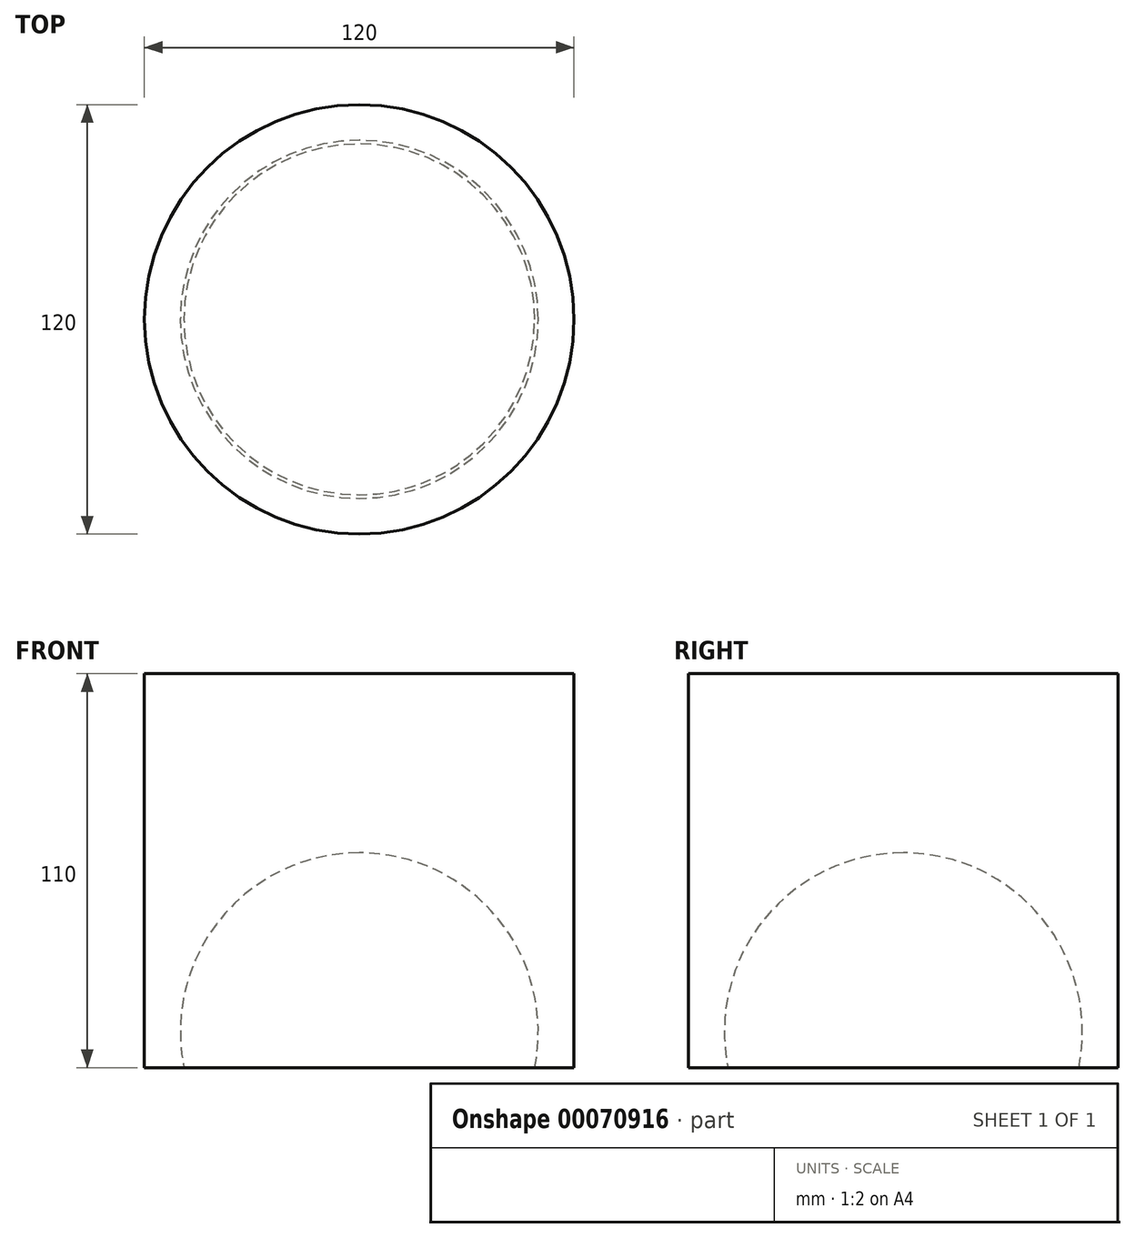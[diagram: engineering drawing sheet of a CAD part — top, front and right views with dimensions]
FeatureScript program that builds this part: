
annotation { "Feature Type Name" : "Feature", "Feature Type Description" : "" }
export const myFeature = defineFeature(function(context is Context, id is Id, definition is map)
    precondition{}
    {
        {
            var Q0;
            Q0=qCreatedBy(makeId("Front.planeOp"),FACE);
            var sketch = newSketch(context, id + "F0", { "sketchPlane" : qUnion([Q0])});
            skArc(sketch, "E0", {"start": v(-50, 0) * mm, "mid": v(0, 50) * mm, "end": v(50, 0) * mm});
            skLineSegment(sketch, "E1", {"start": v(-50, 0) * mm, "end": v(-60, 0) * mm});
            skLineSegment(sketch, "E2", {"start": v(-60, 0) * mm, "end": v(-60, 100) * mm});
            skLineSegment(sketch, "E3", {"start": v(50, 0) * mm, "end": v(60, 0) * mm});
            skLineSegment(sketch, "E4", {"start": v(60, 0) * mm, "end": v(60, 100) * mm});
            skLineSegment(sketch, "E5", {"start": v(60, 100) * mm, "end": v(-60, 100) * mm});
            skLineSegment(sketch, "E6", {"start": v(0, 0) * mm, "end": v(0, 119.73) * mm});
            skCircle(sketch, "E7", {"center": v(0, 0) * mm, "radius": 50 * mm, "construction": true});
            skArc(sketch, "E8", {"start": v(-50, 0) * mm, "mid": v(-49.75, -5.03) * mm, "end": v(-48.99, -10) * mm});
            skArc(sketch, "E9", {"start": v(50, 0) * mm, "mid": v(49.75, -5) * mm, "end": v(49, -9.95) * mm});
            skLineSegment(sketch, "E10", {"start": v(-60, 0) * mm, "end": v(-60, -10) * mm});
            skLineSegment(sketch, "E11", {"start": v(-60, -10) * mm, "end": v(-48.99, -10) * mm});
            skLineSegment(sketch, "E12", {"start": v(60, 0) * mm, "end": v(60, -9.95) * mm});
            skLineSegment(sketch, "E13", {"start": v(60, -9.95) * mm, "end": v(49, -9.95) * mm});
            skSolve(sketch);
        }
        {
            var Q0;
            {var subQ4=sQuery(id+"F0.wireOp",EDGE,"E1");Q0=makeQuery(id+"F0.imprint","IMPRINT",FACE,{"disambiguationData":[TD([[makeQuery(id+"F0.imprint","IMPRINT",EDGE,{"derivedFrom":subQ4}),-1.0]])]});}
            var Q1;
            Q1=makeQuery(id+"F0.imprint","IMPRINT",FACE,{"disambiguationData":[TD([[makeQuery(id+"F0.imprint","IMPRINT",EDGE,{"derivedFrom":sQuery(id+"F0.wireOp",EDGE,"E1")}),1.0]])]});
            var Q2;
            Q2=sQuery(id+"F0.wireOp",EDGE,"E6");
            revolve(context, id + "F1", {"entities" : qUnion([Q0, Q1]), "axis" : qUnion([Q2]), "revolveType" : RevolveType.FULL});
        }
    });
